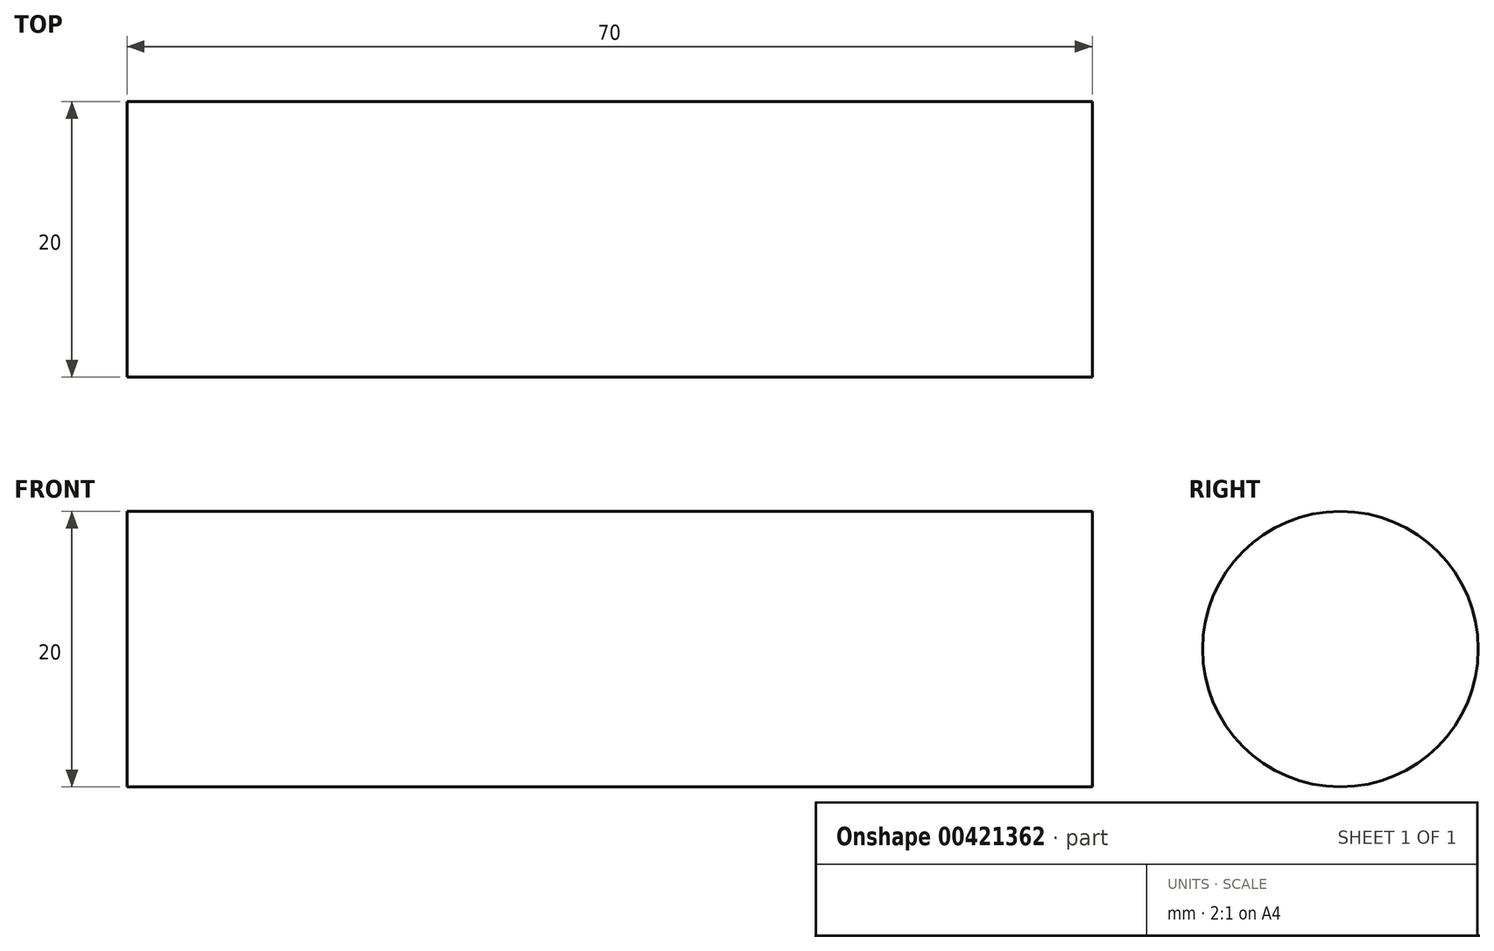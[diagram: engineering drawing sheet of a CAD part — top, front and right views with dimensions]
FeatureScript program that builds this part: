
annotation { "Feature Type Name" : "Feature", "Feature Type Description" : "" }
export const myFeature = defineFeature(function(context is Context, id is Id, definition is map)
    precondition{}
    {
        {
            var Q0;
            Q0=qCreatedBy(makeId("Right.planeOp"),FACE);
            var sketch = newSketch(context, id + "F0", { "sketchPlane" : qUnion([Q0])});
            skCircle(sketch, "E0", {"center": v(0, 0) * mm, "radius": 10 * mm});
            skSolve(sketch);
        }
        {
            var Q0;
            Q0 = qSketchRegion(id + "F0", true);
            extrude(context, id + "F1", {"entities" : qUnion([Q0]), "depth" : 70 * mm});
        }
    });
